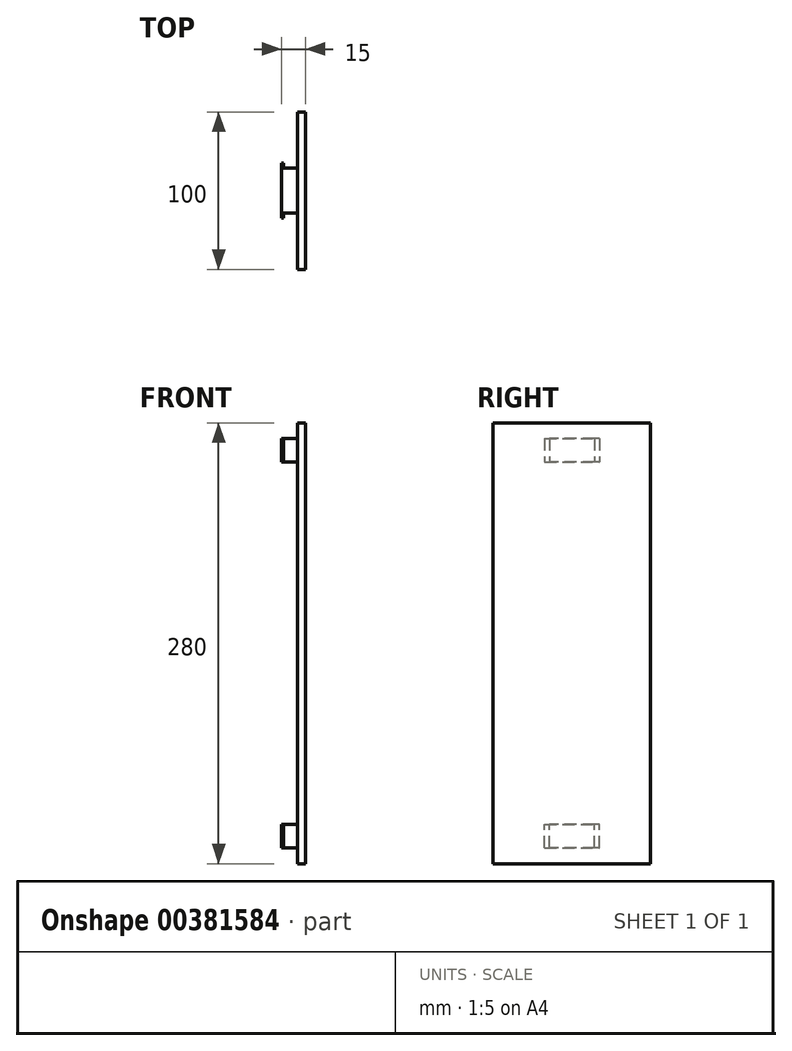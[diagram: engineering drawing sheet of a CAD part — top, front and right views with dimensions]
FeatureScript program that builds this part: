
annotation { "Feature Type Name" : "Feature", "Feature Type Description" : "" }
export const myFeature = defineFeature(function(context is Context, id is Id, definition is map)
    precondition{}
    {
        {
            var Q0;
            Q0=qCreatedBy(makeId("Top.planeOp"),FACE);
            var sketch = newSketch(context, id + "F0", { "sketchPlane" : qUnion([Q0])});
            skLineSegment(sketch, "E0", {"start": v(0, 0) * mm, "end": v(0, 17.4) * mm});
            skLineSegment(sketch, "E1", {"start": v(0, 17.4) * mm, "end": v(1.25, 17.4) * mm});
            skLineSegment(sketch, "E2", {"start": v(1.25, 17.4) * mm, "end": v(1.25, 14.4) * mm});
            skLineSegment(sketch, "E3", {"start": v(1.25, 14.4) * mm, "end": v(10, 14.4) * mm});
            skLineSegment(sketch, "E4", {"start": v(10, 14.4) * mm, "end": v(10, 50) * mm});
            skLineSegment(sketch, "E5", {"start": v(10, 50) * mm, "end": v(15, 50) * mm});
            skLineSegment(sketch, "E6", {"start": v(15, 50) * mm, "end": v(15, 0) * mm});
            skLineSegment(sketch, "E7", {"start": v(0, 0) * mm, "end": v(15, 0) * mm, "construction": true});
            skLineSegment(sketch, "E8.MirrorCS", {"start": v(10, -50) * mm, "end": v(15, -50) * mm});
            skLineSegment(sketch, "E9.MirrorCS", {"start": v(15, -50) * mm, "end": v(15, 0) * mm});
            skLineSegment(sketch, "E10.MirrorCS", {"start": v(10, -14.4) * mm, "end": v(10, -50) * mm});
            skLineSegment(sketch, "E11.MirrorCS", {"start": v(0, 0) * mm, "end": v(0, -17.4) * mm});
            skLineSegment(sketch, "E12.MirrorCS", {"start": v(1.25, -14.4) * mm, "end": v(10, -14.4) * mm});
            skLineSegment(sketch, "E13.MirrorCS", {"start": v(1.25, -17.4) * mm, "end": v(1.25, -14.4) * mm});
            skLineSegment(sketch, "E14.MirrorCS", {"start": v(0, -17.4) * mm, "end": v(1.25, -17.4) * mm});
            skLineSegment(sketch, "E15", {"start": v(10, 14.4) * mm, "end": v(10, -14.4) * mm});
            skSolve(sketch);
        }
        {
            var Q0;
            Q0=makeQuery(id+"F0.imprint","IMPRINT",FACE,{"disambiguationData":[TD([[makeQuery(id+"F0.imprint","IMPRINT",EDGE,{"derivedFrom":sQuery(id+"F0.wireOp",EDGE,"E0")}),-1.0]])]});
            extrude(context, id + "F1", {"entities" : qUnion([Q0]), "oppositeDirection" : true, "depth" : 30 * mm, "offsetDistance" : 25 * mm, "hasSecondDirection" : true, "secondDirectionOppositeDirection" : true, "secondDirectionDepth" : 15 * mm});
        }
        {
            var Q0;
            Q0=makeQuery(id+"F0.imprint","IMPRINT",FACE,{"disambiguationData":[TD([[makeQuery(id+"F0.imprint","IMPRINT",EDGE,{"derivedFrom":sQuery(id+"F0.wireOp",EDGE,"E4")}),-1.0]])]});
            extrude(context, id + "F2", {"entities" : qUnion([Q0]), "operationType" : NewBodyOperationType.ADD, "depth" : 240 * mm, "offsetDistance" : 25 * mm, "hasSecondDirection" : true, "secondDirectionOppositeDirection" : true, "secondDirectionDepth" : 40 * mm});
        }
        {
            var Q0;
            Q0=makeQuery(id+"F0.imprint","IMPRINT",FACE,{"disambiguationData":[TD([[makeQuery(id+"F0.imprint","IMPRINT",EDGE,{"derivedFrom":sQuery(id+"F0.wireOp",EDGE,"E0")}),-1.0]])]});
            extrude(context, id + "F3", {"entities" : qUnion([Q0]), "operationType" : NewBodyOperationType.ADD, "depth" : 230 * mm, "offsetDistance" : 25 * mm, "hasSecondDirection" : true, "secondDirectionOppositeDirection" : false, "secondDirectionDepth" : 215 * mm});
        }
    });
